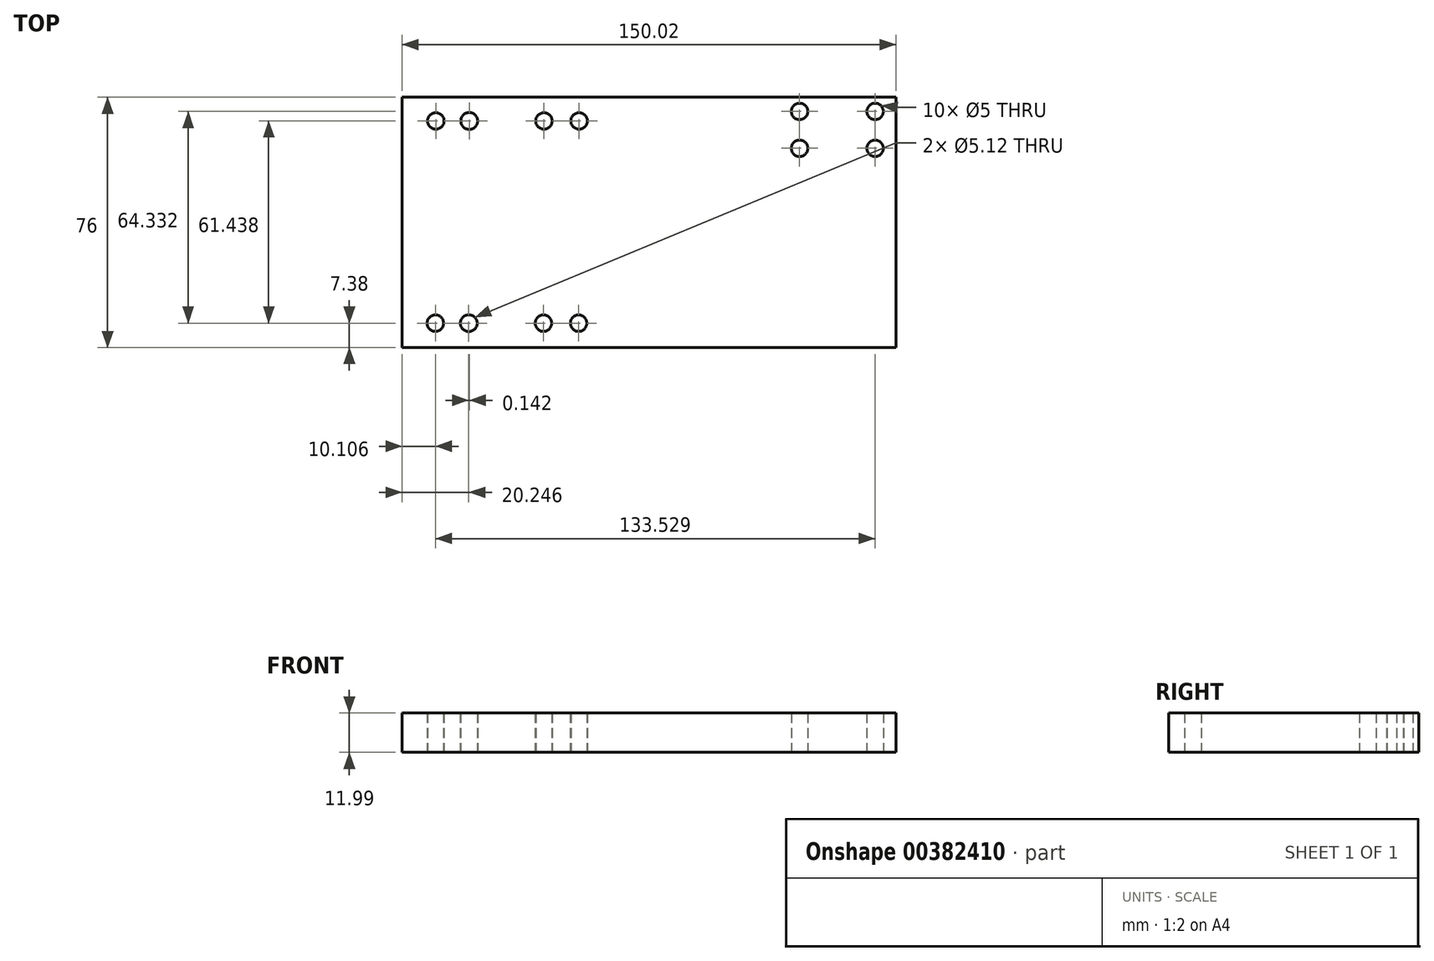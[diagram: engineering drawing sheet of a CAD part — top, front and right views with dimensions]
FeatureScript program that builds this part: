
annotation { "Feature Type Name" : "Feature", "Feature Type Description" : "" }
export const myFeature = defineFeature(function(context is Context, id is Id, definition is map)
    precondition{}
    {
        {
            var Q0;
            Q0=qCreatedBy(makeId("Top.planeOp"),FACE);
            var sketch = newSketch(context, id + "F0", { "sketchPlane" : qUnion([Q0])});
            skLineSegment(sketch, "E0.bottom", {"start": v(-75, 38) * mm, "end": v(75, 38) * mm});
            skLineSegment(sketch, "E0.top", {"start": v(-75, -38) * mm, "end": v(75, -38) * mm});
            skLineSegment(sketch, "E0.left", {"start": v(-75, 38) * mm, "end": v(-75, -38) * mm});
            skLineSegment(sketch, "E0.right", {"start": v(75, 38) * mm, "end": v(75, -38) * mm});
            skPoint(sketch, "E0.middle", {"position": v(0, 0) * mm});
            skCircle(sketch, "E1", {"center": v(-64.76, 30.82) * mm, "radius": 2.5 * mm});
            skCircle(sketch, "E2", {"center": v(-54.62, 30.82) * mm, "radius": 2.56 * mm});
            skCircle(sketch, "E3", {"center": v(-31.94, 30.82) * mm, "radius": 2.5 * mm});
            skCircle(sketch, "E4", {"center": v(-21.27, 30.82) * mm, "radius": 2.5 * mm});
            skCircle(sketch, "E5", {"center": v(-64.9, -30.62) * mm, "radius": 2.5 * mm});
            skCircle(sketch, "E6", {"center": v(-54.76, -30.62) * mm, "radius": 2.56 * mm});
            skCircle(sketch, "E7", {"center": v(-32.08, -30.62) * mm, "radius": 2.5 * mm});
            skCircle(sketch, "E8", {"center": v(-21.4, -30.62) * mm, "radius": 2.5 * mm});
            skCircle(sketch, "E9", {"center": v(45.67, 33.71) * mm, "radius": 2.5 * mm});
            skCircle(sketch, "E10", {"center": v(45.67, 22.5) * mm, "radius": 2.5 * mm});
            skCircle(sketch, "E11", {"center": v(68.62, 22.5) * mm, "radius": 2.5 * mm});
            skCircle(sketch, "E12", {"center": v(68.62, 33.71) * mm, "radius": 2.5 * mm});
            skSolve(sketch);
        }
        {
            var Q0;
            Q0=makeQuery(id+"F0.imprint","IMPRINT",FACE,{"disambiguationData":[TD([[makeQuery(id+"F0.imprint","IMPRINT",EDGE,{"derivedFrom":sQuery(id+"F0.wireOp",EDGE,"E0.bottom")}),-1.0]])]});
            extrude(context, id + "F1", {"entities" : qUnion([Q0]), "depth" : 12 * mm});
        }
    });
